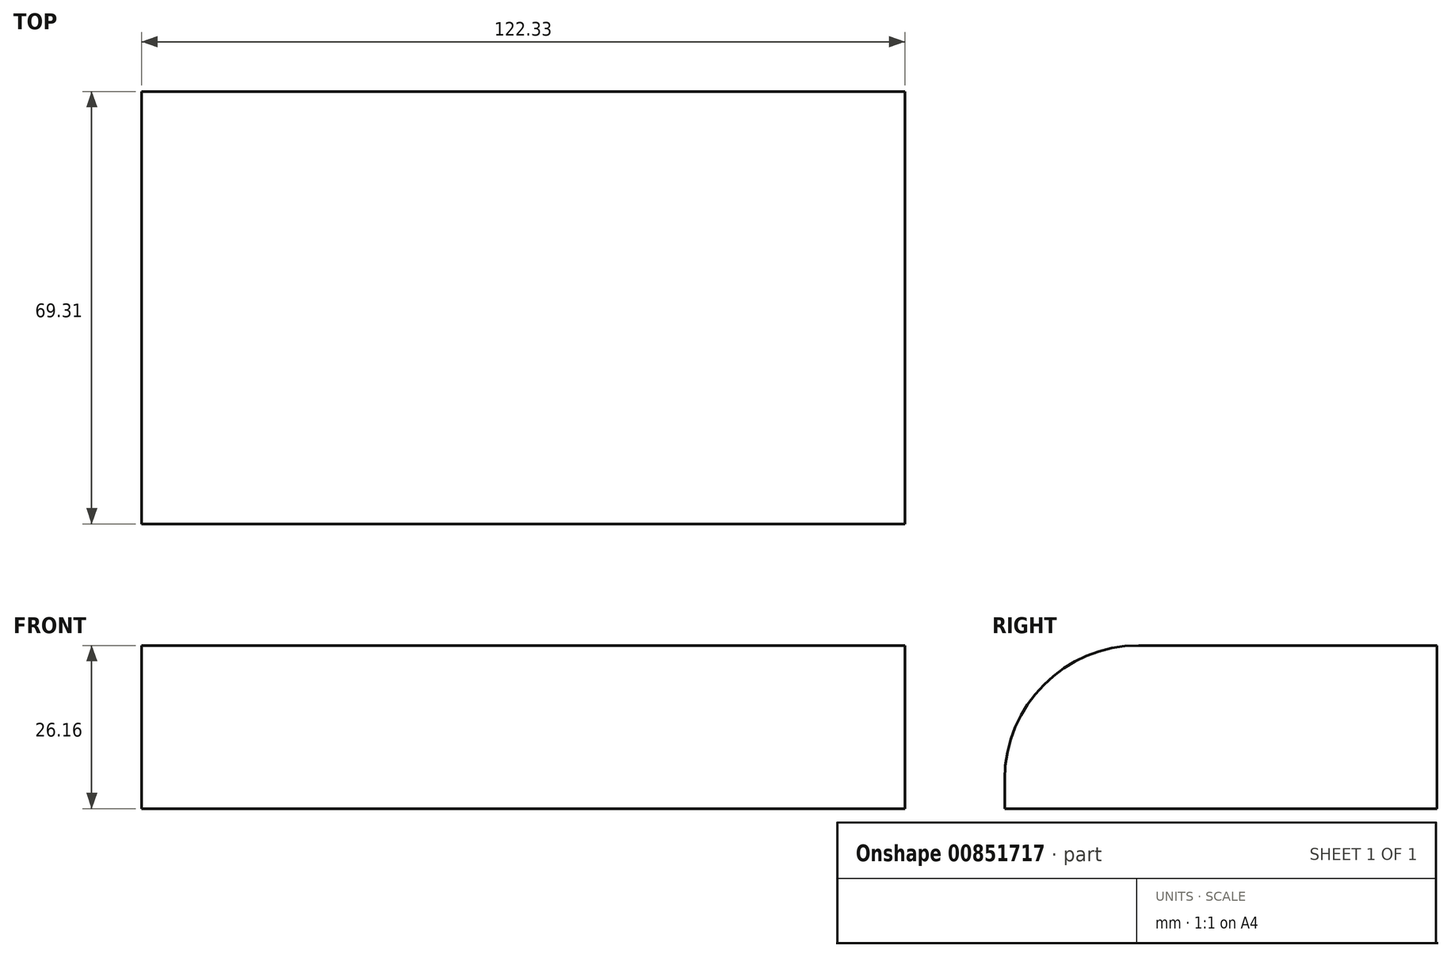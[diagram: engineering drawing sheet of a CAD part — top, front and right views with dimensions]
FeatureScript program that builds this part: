
annotation { "Feature Type Name" : "Feature", "Feature Type Description" : "" }
export const myFeature = defineFeature(function(context is Context, id is Id, definition is map)
    precondition{}
    {
        {
            var Q0;
            Q0=qCreatedBy(makeId("Top.planeOp"),FACE);
            var sketch = newSketch(context, id + "F0", { "sketchPlane" : qUnion([Q0])});
            skLineSegment(sketch, "E0.bottom", {"start": v(-64.23, 32.5) * mm, "end": v(58.1, 32.5) * mm});
            skLineSegment(sketch, "E0.top", {"start": v(-64.23, -36.8) * mm, "end": v(58.1, -36.8) * mm});
            skLineSegment(sketch, "E0.left", {"start": v(-64.23, 32.5) * mm, "end": v(-64.23, -36.8) * mm});
            skLineSegment(sketch, "E0.right", {"start": v(58.1, 32.5) * mm, "end": v(58.1, -36.8) * mm});
            skSolve(sketch);
        }
        {
            var Q0;
            Q0=makeQuery(id+"F0.imprint","IMPRINT",FACE,{"disambiguationData":[TD([[makeQuery(id+"F0.imprint","IMPRINT",EDGE,{"derivedFrom":sQuery(id+"F0.wireOp",EDGE,"E0.bottom")}),-1.0]])]});
            extrude(context, id + "F1", {"entities" : qUnion([Q0]), "depth" : 26.16 * mm, "offsetDistance" : 25.4 * mm});
        }
        {
            var Q0;
            Q0=makeQuery(id+"F1.opExtrude","CAP_EDGE",EDGE,{"disambiguationData":[OSD([sQuery(id+"F0.wireOp",EDGE,"E0.top")])],"isStart":false});
            fillet(context, id + "F2", {"entities" : qUnion([Q0]), "radius" : 21.46 * mm, "tangentPropagation" : true, "allowEdgeOverflow" : false});
        }
    });
